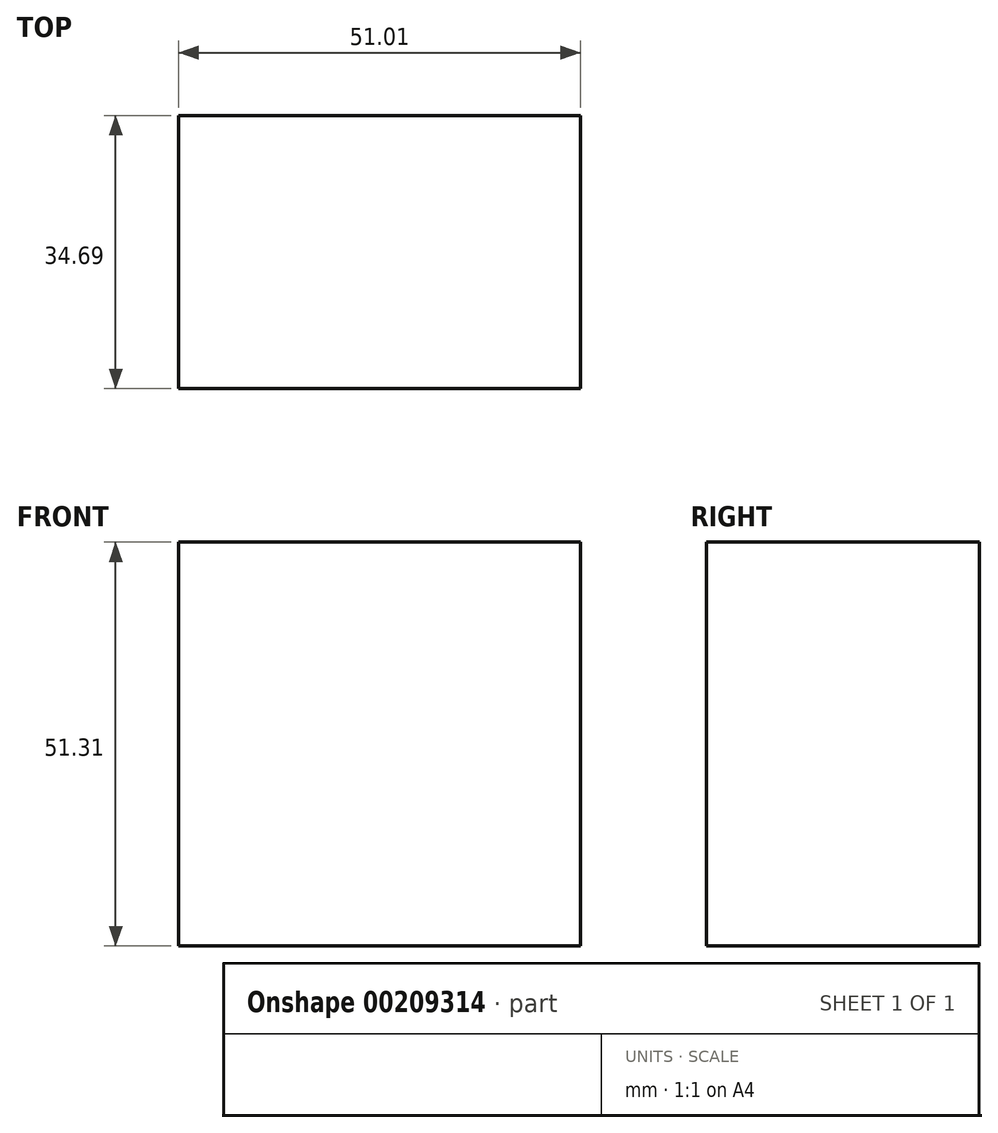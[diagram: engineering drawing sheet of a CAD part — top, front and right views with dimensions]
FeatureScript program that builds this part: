
annotation { "Feature Type Name" : "Feature", "Feature Type Description" : "" }
export const myFeature = defineFeature(function(context is Context, id is Id, definition is map)
    precondition{}
    {
        {
            var Q0;
            Q0=qCreatedBy(makeId("Top.planeOp"),FACE);
            var sketch = newSketch(context, id + "F0", { "sketchPlane" : qUnion([Q0])});
            skLineSegment(sketch, "E0.bottom", {"start": v(-25.65, 16.76) * mm, "end": v(25.36, 16.76) * mm});
            skLineSegment(sketch, "E0.top", {"start": v(-25.65, -17.93) * mm, "end": v(25.36, -17.93) * mm});
            skLineSegment(sketch, "E0.left", {"start": v(-25.65, 16.76) * mm, "end": v(-25.65, -17.93) * mm});
            skLineSegment(sketch, "E0.right", {"start": v(25.36, 16.76) * mm, "end": v(25.36, -17.93) * mm});
            skSolve(sketch);
        }
        {
            var Q0;
            Q0=makeQuery(id+"F0.imprint","IMPRINT",FACE,{"disambiguationData":[TD([[makeQuery(id+"F0.imprint","IMPRINT",EDGE,{"derivedFrom":sQuery(id+"F0.wireOp",EDGE,"E0.bottom")}),-1.0]])]});
            extrude(context, id + "F1", {"entities" : qUnion([Q0]), "depth" : 51.3 * mm});
        }
    });
